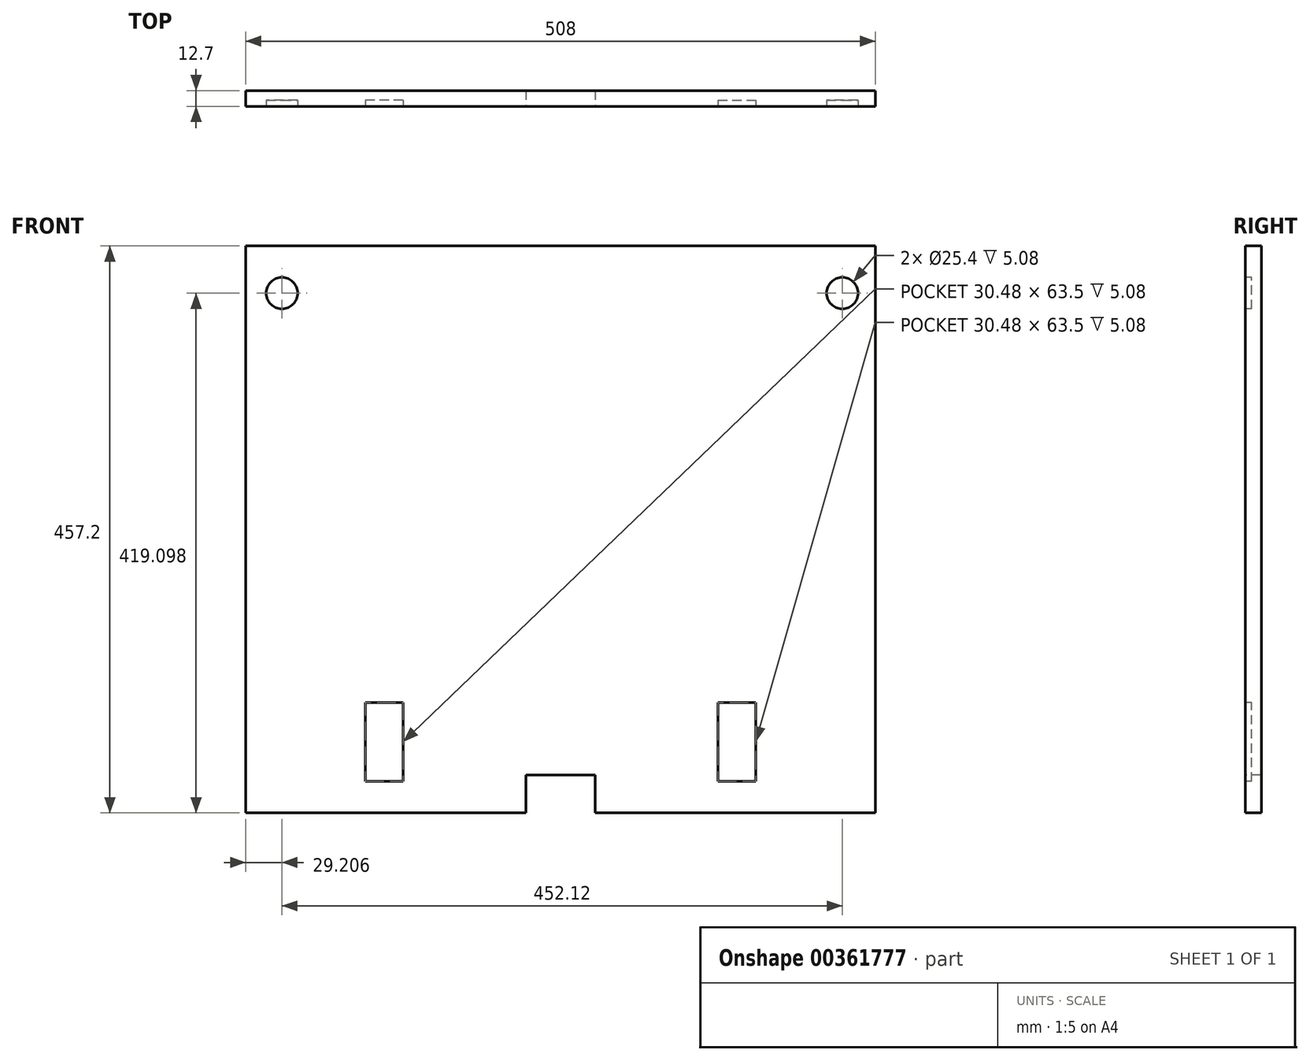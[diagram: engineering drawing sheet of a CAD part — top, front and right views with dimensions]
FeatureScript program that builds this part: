
annotation { "Feature Type Name" : "Feature", "Feature Type Description" : "" }
export const myFeature = defineFeature(function(context is Context, id is Id, definition is map)
    precondition{}
    {
        {
            var Q0;
            Q0=qCreatedBy(makeId("Front.planeOp"),FACE);
            var sketch = newSketch(context, id + "F0", { "sketchPlane" : qUnion([Q0])});
            skLineSegment(sketch, "E0", {"start": v(-237.77, 218.64) * mm, "end": v(270.23, 218.64) * mm});
            skLineSegment(sketch, "E1", {"start": v(270.23, 218.64) * mm, "end": v(270.23, -238.56) * mm});
            skLineSegment(sketch, "E2", {"start": v(270.23, -238.56) * mm, "end": v(-237.77, -238.56) * mm});
            skLineSegment(sketch, "E3", {"start": v(-237.77, -238.56) * mm, "end": v(-237.77, 218.64) * mm});
            skSolve(sketch);
        }
        {
            var Q0;
            Q0=makeQuery(id+"F0.imprint","IMPRINT",FACE,{"disambiguationData":[TD([[makeQuery(id+"F0.imprint","IMPRINT",EDGE,{"derivedFrom":sQuery(id+"F0.wireOp",EDGE,"E0")}),-1.0]])]});
            extrude(context, id + "F1", {"entities" : qUnion([Q0]), "depth" : 12.7 * mm});
        }
        {
            var Q0;
            Q0=makeQuery(id+"F1.opExtrude","CAP_FACE",FACE,{"disambiguationData":[OSD([sQuery(id+"F0.wireOp",EDGE,"E0"),sQuery(id+"F0.wireOp",EDGE,"E1"),sQuery(id+"F0.wireOp",EDGE,"E2"),sQuery(id+"F0.wireOp",EDGE,"E3")])],"isStart":false});
            var sketch = newSketch(context, id + "F2", { "sketchPlane" : qUnion([Q0])});
            skLineSegment(sketch, "E4", {"start": v(-141.25, -213.16) * mm, "end": v(-141.25, -149.66) * mm});
            skLineSegment(sketch, "E5", {"start": v(173.7, -213.16) * mm, "end": v(173.7, -149.66) * mm});
            skCircle(sketch, "E6", {"center": v(243.56, 180.54) * mm, "radius": 12.7 * mm});
            skCircle(sketch, "E7", {"center": v(-208.56, 180.54) * mm, "radius": 12.7 * mm});
            skLineSegment(sketch, "E8", {"start": v(-141.25, -149.66) * mm, "end": v(-110.77, -149.66) * mm});
            skLineSegment(sketch, "E9", {"start": v(-110.77, -149.66) * mm, "end": v(-110.77, -213.16) * mm});
            skLineSegment(sketch, "E10", {"start": v(-110.77, -213.16) * mm, "end": v(-141.25, -213.16) * mm});
            skLineSegment(sketch, "E11", {"start": v(173.7, -149.66) * mm, "end": v(143.23, -149.66) * mm});
            skLineSegment(sketch, "E12", {"start": v(143.23, -149.66) * mm, "end": v(143.23, -213.16) * mm});
            skLineSegment(sketch, "E13", {"start": v(143.23, -213.16) * mm, "end": v(173.7, -213.16) * mm});
            skLineSegment(sketch, "E14", {"start": v(44.17, -238.56) * mm, "end": v(44.17, -208.08) * mm});
            skLineSegment(sketch, "E15", {"start": v(44.17, -208.08) * mm, "end": v(-11.71, -208.08) * mm});
            skLineSegment(sketch, "E16", {"start": v(-11.71, -208.08) * mm, "end": v(-11.71, -238.56) * mm});
            skSolve(sketch);
        }
        {
            var Q0;
            Q0=makeQuery(id+"F2.imprint","IMPRINT",FACE,{"disambiguationData":[TD([[makeQuery(id+"F2.imprint","IMPRINT",EDGE,{"derivedFrom":sQuery(id+"F2.wireOp",EDGE,"E5")}),1.0]])]});
            var Q1;
            Q1=makeQuery(id+"F2.imprint","IMPRINT",FACE,{"disambiguationData":[TD([[makeQuery(id+"F2.imprint","IMPRINT",EDGE,{"derivedFrom":sQuery(id+"F2.wireOp",EDGE,"E4")}),-1.0]])]});
            extrude(context, id + "F3", {"entities" : qUnion([Q0, Q1]), "operationType" : NewBodyOperationType.REMOVE, "oppositeDirection" : true, "depth" : 5.08 * mm});
        }
        {
            var Q0;
            Q0=makeQuery(id+"F2.imprint","IMPRINT",FACE,{"disambiguationData":[TD([[makeQuery(id+"F2.imprint","IMPRINT",EDGE,{"derivedFrom":sQuery(id+"F2.wireOp",EDGE,"E7")}),1.0]])]});
            var Q1;
            Q1=makeQuery(id+"F2.imprint","IMPRINT",FACE,{"disambiguationData":[TD([[makeQuery(id+"F2.imprint","IMPRINT",EDGE,{"derivedFrom":sQuery(id+"F2.wireOp",EDGE,"E6")}),1.0]])]});
            extrude(context, id + "F4", {"entities" : qUnion([Q0, Q1]), "operationType" : NewBodyOperationType.REMOVE, "oppositeDirection" : true, "depth" : 5.08 * mm});
        }
        {
            var Q0;
            {var subQ0=sQuery(id+"F2.wireOp",EDGE,"E14");Q0=makeQuery(id+"F2.imprint","IMPRINT",FACE,{"disambiguationData":[TD([[makeQuery(id+"F2.imprint","IMPRINT",EDGE,{"derivedFrom":subQ0}),1.0]])]});}
            extrude(context, id + "F5", {"entities" : qUnion([Q0]), "operationType" : NewBodyOperationType.REMOVE, "oppositeDirection" : true, "depth" : 12.7 * mm});
        }
    });
